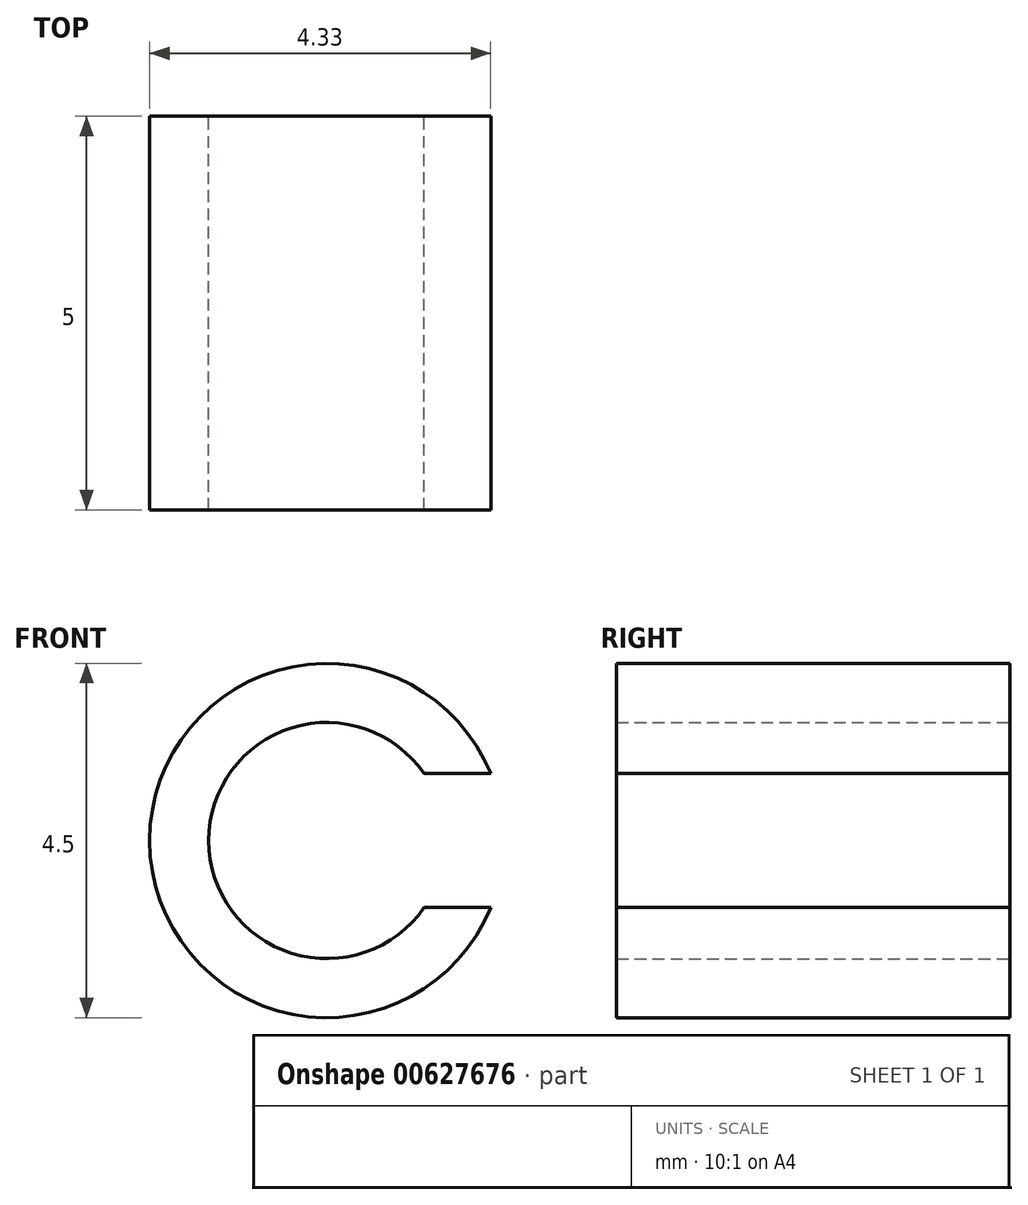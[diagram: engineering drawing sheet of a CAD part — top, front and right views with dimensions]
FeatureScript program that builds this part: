
annotation { "Feature Type Name" : "Feature", "Feature Type Description" : "" }
export const myFeature = defineFeature(function(context is Context, id is Id, definition is map)
    precondition{}
    {
        {
            var Q0;
            Q0=qCreatedBy(makeId("Front.planeOp"),FACE);
            var sketch = newSketch(context, id + "F0", { "sketchPlane" : qUnion([Q0])});
            skArc(sketch, "E0", {"start": v(1.24, 0.85) * mm, "mid": v(-1.5, 0) * mm, "end": v(1.24, -0.85) * mm});
            skArc(sketch, "E1", {"start": v(2.08, 0.85) * mm, "mid": v(-2.25, 0) * mm, "end": v(2.08, -0.85) * mm});
            skLineSegment(sketch, "E2", {"start": v(1.24, 0.85) * mm, "end": v(2.08, 0.85) * mm});
            skLineSegment(sketch, "E3", {"start": v(1.24, -0.85) * mm, "end": v(2.08, -0.85) * mm});
            skSolve(sketch);
        }
        {
            var Q0;
            Q0 = qSketchRegion(id + "F0", true);
            extrude(context, id + "F1", {"entities" : qUnion([Q0]), "depth" : 5 * mm, "offsetDistance" : 25 * mm});
        }
    });
